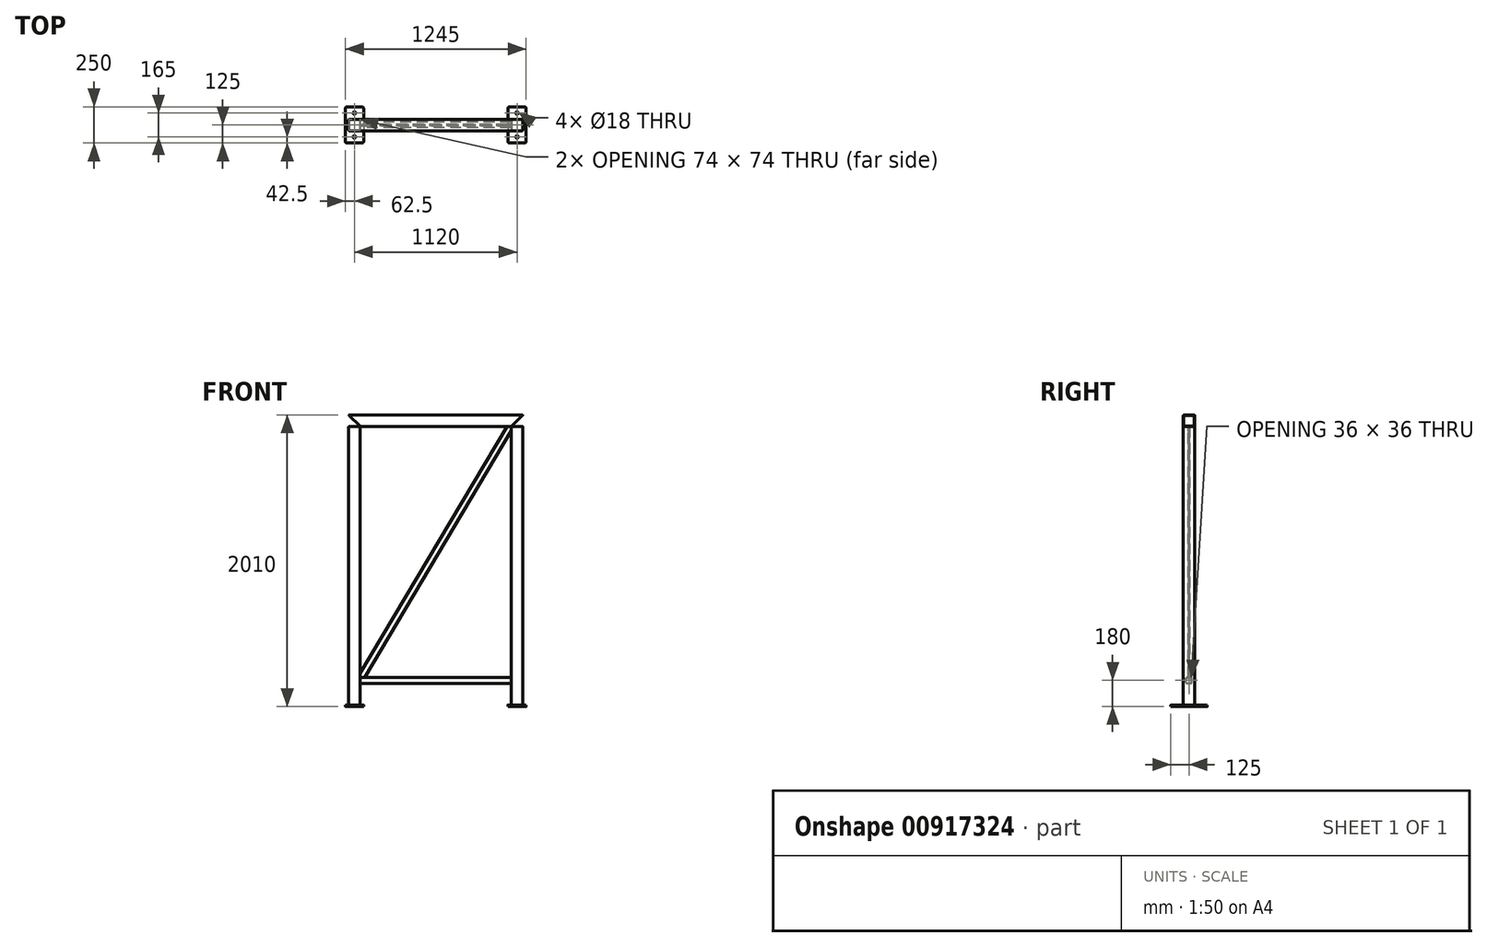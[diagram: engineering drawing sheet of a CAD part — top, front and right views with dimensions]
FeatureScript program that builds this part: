
annotation { "Feature Type Name" : "Feature", "Feature Type Description" : "" }
export const myFeature = defineFeature(function(context is Context, id is Id, definition is map)
    precondition{}
    {
        {
            var Q0;
            Q0=qCreatedBy(makeId("Top.planeOp"),FACE);
            var sketch = newSketch(context, id + "F0", { "sketchPlane" : qUnion([Q0])});
            skLineSegment(sketch, "E0.bottom", {"start": v(-594, -40) * mm, "end": v(-526, -40) * mm});
            skLineSegment(sketch, "E0.top", {"start": v(-594, 40) * mm, "end": v(-526, 40) * mm});
            skLineSegment(sketch, "E0.left", {"start": v(-600, -34) * mm, "end": v(-600, 34) * mm});
            skLineSegment(sketch, "E0.right", {"start": v(-520, -34) * mm, "end": v(-520, 34) * mm});
            skPoint(sketch, "E1.visualSharp", {"position": v(-600, 40) * mm});
            skArc(sketch, "E1.filletArc", {"start": v(-594, 40) * mm, "mid": v(-598.24, 38.24) * mm, "end": v(-600, 34) * mm});
            skPoint(sketch, "E2.visualSharp", {"position": v(-520, 40) * mm});
            skArc(sketch, "E2.filletArc", {"start": v(-520, 34) * mm, "mid": v(-521.76, 38.24) * mm, "end": v(-526, 40) * mm});
            skPoint(sketch, "E3.visualSharp", {"position": v(-520, -40) * mm});
            skArc(sketch, "E3.filletArc", {"start": v(-526, -40) * mm, "mid": v(-521.76, -38.24) * mm, "end": v(-520, -34) * mm});
            skPoint(sketch, "E4.visualSharp", {"position": v(-600, -40) * mm});
            skArc(sketch, "E4.filletArc", {"start": v(-600, -34) * mm, "mid": v(-598.24, -38.24) * mm, "end": v(-594, -40) * mm});
            skArc(sketch, "E5.0", {"start": v(-594, 37) * mm, "mid": v(-596.12, 36.12) * mm, "end": v(-597, 34) * mm});
            skLineSegment(sketch, "E5.1", {"start": v(-597, -34) * mm, "end": v(-597, 34) * mm});
            skLineSegment(sketch, "E5.2", {"start": v(-594, 37) * mm, "end": v(-526, 37) * mm});
            skArc(sketch, "E5.3", {"start": v(-597, -34) * mm, "mid": v(-596.12, -36.12) * mm, "end": v(-594, -37) * mm});
            skArc(sketch, "E5.4", {"start": v(-523, 34) * mm, "mid": v(-523.88, 36.12) * mm, "end": v(-526, 37) * mm});
            skLineSegment(sketch, "E5.5", {"start": v(-523, -34) * mm, "end": v(-523, 34) * mm});
            skArc(sketch, "E5.6", {"start": v(-526, -37) * mm, "mid": v(-523.88, -36.12) * mm, "end": v(-523, -34) * mm});
            skLineSegment(sketch, "E5.7", {"start": v(-594, -37) * mm, "end": v(-526, -37) * mm});
            skArc(sketch, "E6.MirrorCS", {"start": v(594, 37) * mm, "mid": v(596.12, 36.12) * mm, "end": v(597, 34) * mm});
            skArc(sketch, "E7.MirrorCS", {"start": v(600, -34) * mm, "mid": v(598.24, -38.24) * mm, "end": v(594, -40) * mm});
            skArc(sketch, "E8.MirrorCS", {"start": v(597, -34) * mm, "mid": v(596.12, -36.12) * mm, "end": v(594, -37) * mm});
            skArc(sketch, "E9.MirrorCS", {"start": v(526, -40) * mm, "mid": v(521.76, -38.24) * mm, "end": v(520, -34) * mm});
            skArc(sketch, "E10.MirrorCS", {"start": v(594, 40) * mm, "mid": v(598.24, 38.24) * mm, "end": v(600, 34) * mm});
            skArc(sketch, "E11.MirrorCS", {"start": v(523, 34) * mm, "mid": v(523.88, 36.12) * mm, "end": v(526, 37) * mm});
            skArc(sketch, "E12.MirrorCS", {"start": v(526, -37) * mm, "mid": v(523.88, -36.12) * mm, "end": v(523, -34) * mm});
            skArc(sketch, "E13.MirrorCS", {"start": v(520, 34) * mm, "mid": v(521.76, 38.24) * mm, "end": v(526, 40) * mm});
            skLineSegment(sketch, "E14.MirrorCS", {"start": v(594, -40) * mm, "end": v(526, -40) * mm});
            skPoint(sketch, "E15.MirrorP", {"position": v(600, 40) * mm});
            skPoint(sketch, "E16.MirrorP", {"position": v(520, 40) * mm});
            skLineSegment(sketch, "E17.MirrorCS", {"start": v(594, 40) * mm, "end": v(526, 40) * mm});
            skPoint(sketch, "E18.MirrorP", {"position": v(600, -40) * mm});
            skLineSegment(sketch, "E19.MirrorCS", {"start": v(523, -34) * mm, "end": v(523, 34) * mm});
            skLineSegment(sketch, "E20.MirrorCS", {"start": v(597, -34) * mm, "end": v(597, 34) * mm});
            skPoint(sketch, "E21.MirrorP", {"position": v(520, -40) * mm});
            skLineSegment(sketch, "E22.MirrorCS", {"start": v(594, 37) * mm, "end": v(526, 37) * mm});
            skLineSegment(sketch, "E23.MirrorCS", {"start": v(520, -34) * mm, "end": v(520, 34) * mm});
            skLineSegment(sketch, "E24.MirrorCS", {"start": v(594, -37) * mm, "end": v(526, -37) * mm});
            skLineSegment(sketch, "E25.MirrorCS", {"start": v(600, -34) * mm, "end": v(600, 34) * mm});
            skLineSegment(sketch, "E26", {"start": v(0, 0) * mm, "end": v(-520, 0) * mm, "construction": true});
            skSolve(sketch);
        }
        {
            var Q0;
            Q0 = qSketchRegion(id + "F0", true);
            extrude(context, id + "F1", {"entities" : qUnion([Q0]), "endBound" : BoundingType.SYMMETRIC, "depth" : 2000 * mm, "offsetDistance" : 25 * mm});
        }
        {
            var Q0;
            Q0=qCreatedBy(makeId("Right.planeOp"),FACE);
            var sketch = newSketch(context, id + "F2", { "sketchPlane" : qUnion([Q0])});
            skLineSegment(sketch, "E27.bottom", {"start": v(-16, -850) * mm, "end": v(16, -850) * mm});
            skLineSegment(sketch, "E27.top", {"start": v(-16, -810) * mm, "end": v(16, -810) * mm});
            skLineSegment(sketch, "E27.left", {"start": v(-20, -846) * mm, "end": v(-20, -814) * mm});
            skLineSegment(sketch, "E27.right", {"start": v(20, -846) * mm, "end": v(20, -814) * mm});
            skPoint(sketch, "E28.visualSharp", {"position": v(-20, -810) * mm});
            skArc(sketch, "E28.filletArc", {"start": v(-16, -810) * mm, "mid": v(-18.83, -811.17) * mm, "end": v(-20, -814) * mm});
            skPoint(sketch, "E29.visualSharp", {"position": v(20, -810) * mm});
            skArc(sketch, "E29.filletArc", {"start": v(20, -814) * mm, "mid": v(18.83, -811.17) * mm, "end": v(16, -810) * mm});
            skPoint(sketch, "E30.visualSharp", {"position": v(20, -850) * mm});
            skArc(sketch, "E30.filletArc", {"start": v(16, -850) * mm, "mid": v(18.83, -848.83) * mm, "end": v(20, -846) * mm});
            skPoint(sketch, "E31.visualSharp", {"position": v(-20, -850) * mm});
            skArc(sketch, "E31.filletArc", {"start": v(-20, -846) * mm, "mid": v(-18.83, -848.83) * mm, "end": v(-16, -850) * mm});
            skLineSegment(sketch, "E32.0", {"start": v(-16, -812) * mm, "end": v(16, -812) * mm});
            skArc(sketch, "E32.1", {"start": v(18, -814) * mm, "mid": v(17.41, -812.59) * mm, "end": v(16, -812) * mm});
            skArc(sketch, "E32.2", {"start": v(-16, -812) * mm, "mid": v(-17.41, -812.59) * mm, "end": v(-18, -814) * mm});
            skLineSegment(sketch, "E32.3", {"start": v(18, -846) * mm, "end": v(18, -814) * mm});
            skLineSegment(sketch, "E32.4", {"start": v(-18, -846) * mm, "end": v(-18, -814) * mm});
            skArc(sketch, "E32.5", {"start": v(-18, -846) * mm, "mid": v(-17.41, -847.41) * mm, "end": v(-16, -848) * mm});
            skLineSegment(sketch, "E32.6", {"start": v(-16, -848) * mm, "end": v(16, -848) * mm});
            skArc(sketch, "E32.7", {"start": v(16, -848) * mm, "mid": v(17.41, -847.41) * mm, "end": v(18, -846) * mm});
            skLineSegment(sketch, "E33", {"start": v(0, -850) * mm, "end": v(0, -1000) * mm, "construction": true});
            skSolve(sketch);
        }
        {
            var Q0;
            Q0 = qSketchRegion(id + "F2", true);
            extrude(context, id + "F3", {"entities" : qUnion([Q0]), "endBound" : BoundingType.SYMMETRIC, "depth" : 1040 * mm, "offsetDistance" : 25 * mm});
        }
        {
            var Q0;
            Q0=makeQuery(id+"F1.opExtrude","SWEPT_FACE",FACE,{"disambiguationData":[OSD([sQuery(id+"F0.wireOp",EDGE,"E0.bottom")])]});
            var sketch = newSketch(context, id + "F4", { "sketchPlane" : qUnion([Q0])});
            skLineSegment(sketch, "E34", {"start": v(-600, 1000) * mm, "end": v(-520, 920) * mm});
            skLineSegment(sketch, "E35", {"start": v(-520, 920) * mm, "end": v(-520, 1000) * mm});
            skLineSegment(sketch, "E36", {"start": v(-520, 1000) * mm, "end": v(-600, 1000) * mm});
            skLineSegment(sketch, "E37", {"start": v(600, 1000) * mm, "end": v(520, 1000) * mm});
            skLineSegment(sketch, "E38", {"start": v(520, 1000) * mm, "end": v(520, 920) * mm});
            skLineSegment(sketch, "E39", {"start": v(520, 920) * mm, "end": v(600, 1000) * mm});
            skSolve(sketch);
        }
        {
            var Q0;
            Q0 = qSketchRegion(id + "F4", true);
            extrude(context, id + "F5", {"entities" : qUnion([Q0]), "operationType" : NewBodyOperationType.REMOVE, "endBound" : BoundingType.THROUGH_ALL, "oppositeDirection" : true, "depth" : 25 * mm, "offsetDistance" : 25 * mm});
        }
        {
            var Q0;
            Q0=qCreatedBy(makeId("Right.planeOp"),FACE);
            var sketch = newSketch(context, id + "F6", { "sketchPlane" : qUnion([Q0])});
            skLineSegment(sketch, "E40.bottom", {"start": v(34, 1000) * mm, "end": v(-34, 1000) * mm});
            skLineSegment(sketch, "E40.top", {"start": v(34, 920) * mm, "end": v(-34, 920) * mm});
            skLineSegment(sketch, "E40.left", {"start": v(40, 994) * mm, "end": v(40, 926) * mm});
            skLineSegment(sketch, "E40.right", {"start": v(-40, 994) * mm, "end": v(-40, 926) * mm});
            skArc(sketch, "E41.filletArc", {"start": v(40, 994) * mm, "mid": v(38.24, 998.24) * mm, "end": v(34, 1000) * mm});
            skArc(sketch, "E42.filletArc", {"start": v(-34, 1000) * mm, "mid": v(-38.24, 998.24) * mm, "end": v(-40, 994) * mm});
            skArc(sketch, "E43.filletArc", {"start": v(-40, 926) * mm, "mid": v(-38.24, 921.76) * mm, "end": v(-34, 920) * mm});
            skArc(sketch, "E44.filletArc", {"start": v(34, 920) * mm, "mid": v(38.24, 921.76) * mm, "end": v(40, 926) * mm});
            skArc(sketch, "E45.0", {"start": v(37, 994) * mm, "mid": v(36.12, 996.12) * mm, "end": v(34, 997) * mm});
            skLineSegment(sketch, "E45.1", {"start": v(37, 994) * mm, "end": v(37, 926) * mm});
            skLineSegment(sketch, "E45.2", {"start": v(34, 997) * mm, "end": v(-34, 997) * mm});
            skArc(sketch, "E45.3", {"start": v(34, 923) * mm, "mid": v(36.12, 923.88) * mm, "end": v(37, 926) * mm});
            skArc(sketch, "E45.4", {"start": v(-34, 997) * mm, "mid": v(-36.12, 996.12) * mm, "end": v(-37, 994) * mm});
            skLineSegment(sketch, "E45.5", {"start": v(-37, 994) * mm, "end": v(-37, 926) * mm});
            skArc(sketch, "E45.6", {"start": v(-37, 926) * mm, "mid": v(-36.12, 923.88) * mm, "end": v(-34, 923) * mm});
            skLineSegment(sketch, "E45.7", {"start": v(34, 923) * mm, "end": v(-34, 923) * mm});
            skLineSegment(sketch, "E46", {"start": v(0, 923) * mm, "end": v(0, 1000) * mm, "construction": true});
            skSolve(sketch);
        }
        {
            var Q0;
            Q0 = qSketchRegion(id + "F6", true);
            extrude(context, id + "F7", {"entities" : qUnion([Q0]), "endBound" : BoundingType.SYMMETRIC, "depth" : 1200 * mm, "offsetDistance" : 25 * mm});
        }
        {
            var Q0;
            Q0=makeQuery(id+"F7.opExtrude","SWEPT_FACE",FACE,{"disambiguationData":[OSD([sQuery(id+"F6.wireOp",EDGE,"E40.right")])]});
            var sketch = newSketch(context, id + "F8", { "sketchPlane" : qUnion([Q0])});
            skLineSegment(sketch, "E47", {"start": v(-600, 920) * mm, "end": v(-600, 1000) * mm});
            skLineSegment(sketch, "E48", {"start": v(-600, 1000) * mm, "end": v(-520, 920) * mm});
            skLineSegment(sketch, "E49", {"start": v(-520, 920) * mm, "end": v(-600, 920) * mm});
            skLineSegment(sketch, "E50", {"start": v(520, 920) * mm, "end": v(600, 920) * mm});
            skLineSegment(sketch, "E51", {"start": v(600, 920) * mm, "end": v(600, 1000) * mm});
            skLineSegment(sketch, "E52", {"start": v(600, 1000) * mm, "end": v(520, 920) * mm});
            skSolve(sketch);
        }
        {
            var Q0;
            Q0 = qSketchRegion(id + "F8", true);
            extrude(context, id + "F9", {"entities" : qUnion([Q0]), "operationType" : NewBodyOperationType.REMOVE, "endBound" : BoundingType.THROUGH_ALL, "oppositeDirection" : true, "depth" : 25 * mm, "offsetDistance" : 25 * mm});
        }
        {
            var Q0;
            Q0=qCreatedBy(makeId("Front.planeOp"),FACE);
            var sketch = newSketch(context, id + "F10", { "sketchPlane" : qUnion([Q0])});
            skLineSegment(sketch, "E53", {"start": v(490.81, 920) * mm, "end": v(-520, -780.81) * mm});
            skLineSegment(sketch, "E54", {"start": v(-520, -780.81) * mm, "end": v(-520, -810) * mm});
            skLineSegment(sketch, "E55", {"start": v(-520, -810) * mm, "end": v(-490.81, -810) * mm});
            skLineSegment(sketch, "E56", {"start": v(-490.81, -810) * mm, "end": v(520, 890.81) * mm});
            skLineSegment(sketch, "E57", {"start": v(520, 890.81) * mm, "end": v(520, 920) * mm});
            skLineSegment(sketch, "E58", {"start": v(520, 920) * mm, "end": v(490.81, 920) * mm});
            skSolve(sketch);
        }
        {
            var Q0;
            Q0 = qSketchRegion(id + "F10", true);
            extrude(context, id + "F11", {"entities" : qUnion([Q0]), "endBound" : BoundingType.SYMMETRIC, "depth" : 10 * mm, "offsetDistance" : 25 * mm});
        }
        {
            var Q0;
            Q0=makeQuery(id+"F1.opExtrude","CAP_FACE",FACE,{"disambiguationData":[OSD([sQuery(id+"F0.wireOp",EDGE,"E0.bottom"),sQuery(id+"F0.wireOp",EDGE,"E0.top"),sQuery(id+"F0.wireOp",EDGE,"E0.left"),sQuery(id+"F0.wireOp",EDGE,"E0.right"),sQuery(id+"F0.wireOp",EDGE,"E1.filletArc"),sQuery(id+"F0.wireOp",EDGE,"E2.filletArc"),sQuery(id+"F0.wireOp",EDGE,"E3.filletArc"),sQuery(id+"F0.wireOp",EDGE,"E4.filletArc"),sQuery(id+"F0.wireOp",EDGE,"E5.0"),sQuery(id+"F0.wireOp",EDGE,"E5.1"),sQuery(id+"F0.wireOp",EDGE,"E5.2"),sQuery(id+"F0.wireOp",EDGE,"E5.3"),sQuery(id+"F0.wireOp",EDGE,"E5.4"),sQuery(id+"F0.wireOp",EDGE,"E5.5"),sQuery(id+"F0.wireOp",EDGE,"E5.6"),sQuery(id+"F0.wireOp",EDGE,"E5.7")])],"isStart":true});
            var sketch = newSketch(context, id + "F12", { "sketchPlane" : qUnion([Q0])});
            skLineSegment(sketch, "E59.bottom", {"start": v(-507.5, -125) * mm, "end": v(-612.5, -125) * mm});
            skLineSegment(sketch, "E59.top", {"start": v(-507.5, 125) * mm, "end": v(-612.5, 125) * mm});
            skLineSegment(sketch, "E59.left", {"start": v(-497.5, -115) * mm, "end": v(-497.5, 115) * mm});
            skLineSegment(sketch, "E59.right", {"start": v(-622.5, -115) * mm, "end": v(-622.5, 115) * mm});
            skLineSegment(sketch, "E60", {"start": v(-560, -125) * mm, "end": v(-560, -40) * mm, "construction": true});
            skLineSegment(sketch, "E61", {"start": v(-560, 40) * mm, "end": v(-560, 125) * mm, "construction": true});
            skPoint(sketch, "E62.visualSharp", {"position": v(-622.5, -125) * mm});
            skArc(sketch, "E62.filletArc", {"start": v(-622.5, -115) * mm, "mid": v(-619.57, -122.07) * mm, "end": v(-612.5, -125) * mm});
            skPoint(sketch, "E63.visualSharp", {"position": v(-622.5, 125) * mm});
            skArc(sketch, "E63.filletArc", {"start": v(-612.5, 125) * mm, "mid": v(-619.57, 122.07) * mm, "end": v(-622.5, 115) * mm});
            skPoint(sketch, "E64.visualSharp", {"position": v(-497.5, 125) * mm});
            skArc(sketch, "E64.filletArc", {"start": v(-497.5, 115) * mm, "mid": v(-500.43, 122.07) * mm, "end": v(-507.5, 125) * mm});
            skPoint(sketch, "E65.visualSharp", {"position": v(-497.5, -125) * mm});
            skArc(sketch, "E65.filletArc", {"start": v(-507.5, -125) * mm, "mid": v(-500.43, -122.07) * mm, "end": v(-497.5, -115) * mm});
            skCircle(sketch, "E66", {"center": v(-560, -82.5) * mm, "radius": 9 * mm});
            skCircle(sketch, "E67", {"center": v(-560, 82.5) * mm, "radius": 9 * mm});
            skSolve(sketch);
        }
        {
            var Q0;
            Q0 = qSketchRegion(id + "F12", true);
            extrude(context, id + "F13", {"entities" : qUnion([Q0]), "depth" : 10 * mm, "offsetDistance" : 25 * mm});
        }
        {
            var Q0;
            Q0=makeQuery(id+"F13.opExtrude","SWEPT_BODY",BODY,{"disambiguationData":[OSD([sQuery(id+"F12.wireOp",EDGE,"E59.bottom"),sQuery(id+"F12.wireOp",EDGE,"E59.top"),sQuery(id+"F12.wireOp",EDGE,"E59.left"),sQuery(id+"F12.wireOp",EDGE,"E59.right"),sQuery(id+"F12.wireOp",EDGE,"E62.filletArc"),sQuery(id+"F12.wireOp",EDGE,"E63.filletArc"),sQuery(id+"F12.wireOp",EDGE,"E64.filletArc"),sQuery(id+"F12.wireOp",EDGE,"E65.filletArc"),sQuery(id+"F12.wireOp",EDGE,"E66"),sQuery(id+"F12.wireOp",EDGE,"E67")])]});
            var Q1;
            Q1=qCreatedBy(makeId("Right.planeOp"),FACE);
            mirror(context, id + "F14", {"entities" : qUnion([Q0]), "mirrorPlane" : qUnion([Q1])});
        }
    });
